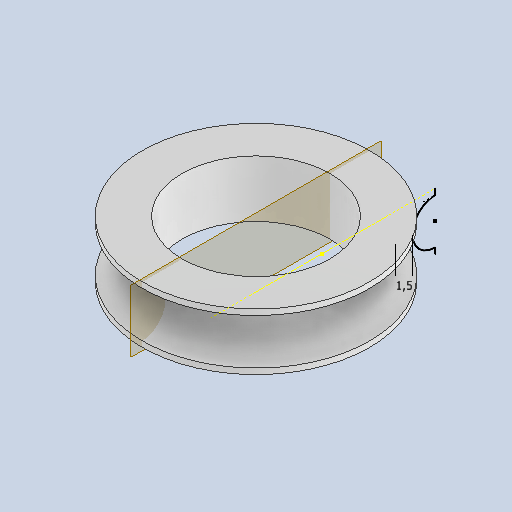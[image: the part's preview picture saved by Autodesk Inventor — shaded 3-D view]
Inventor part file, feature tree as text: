
AUTODESK INVENTOR PART (.ipt)
format: ipt  version: 2025 (Build 290162010, 162A)  size: 166,400 bytes
history: native  units: mm
features: other x4, sketch x3, reference x2, plane x1, sweep x1
ambient origin geometry x8: Origin, YZ Plane, XZ Plane, XY Plane, X Axis, Y Axis, Z Axis, Center Point
bodies: Body1 (feature_tree)
feature tree (11):
  sketch  "Skizze1"  dims[d0=20.0mm d4=1.5mm]
  sketch  "Skizze2"  dims[d7=0.0mm d8=0.0mm]
  plane  "Arbeitsebene1"
  sweep  "Sweeping2"
  reference  "Referenz1"
  sketch  "Skizze3"  dims[d9=8.0mm]
  reference  "Referenz2"
  other  "<userpath>\GIT\HDVKBM\CAD\Krandemonstrator\Umlenkrolle.iam"
  other  "Umlenkrolle.iam"
  other  "Lager:1"
  other  "DIN 625 SKF SKF 624:1"
